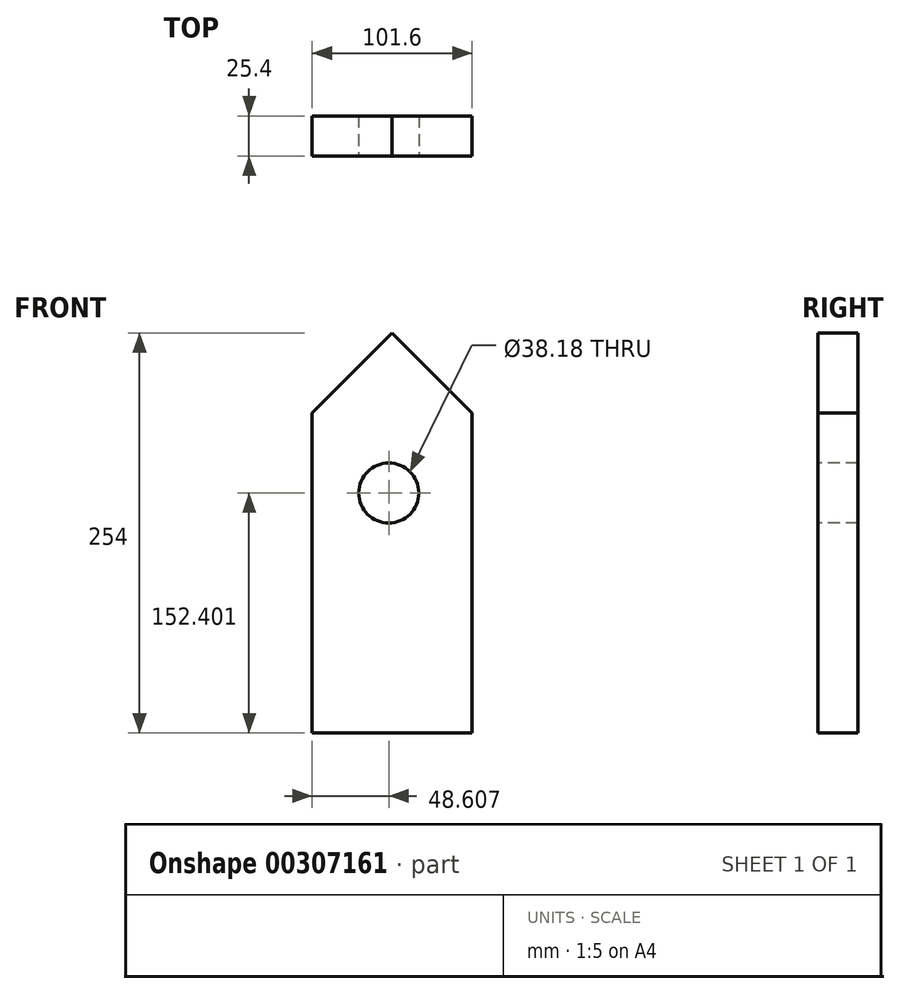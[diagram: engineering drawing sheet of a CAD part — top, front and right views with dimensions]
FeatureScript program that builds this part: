
annotation { "Feature Type Name" : "Feature", "Feature Type Description" : "" }
export const myFeature = defineFeature(function(context is Context, id is Id, definition is map)
    precondition{}
    {
        {
            var Q0;
            Q0=qCreatedBy(makeId("Front.planeOp"),FACE);
            var sketch = newSketch(context, id + "F0", { "sketchPlane" : qUnion([Q0])});
            skLineSegment(sketch, "E0", {"start": v(-46.78, -67.94) * mm, "end": v(54.82, -67.94) * mm});
            skLineSegment(sketch, "E1", {"start": v(54.82, -67.94) * mm, "end": v(54.82, 135.26) * mm});
            skLineSegment(sketch, "E2", {"start": v(-46.78, -67.94) * mm, "end": v(-46.78, 135.26) * mm});
            skLineSegment(sketch, "E3", {"start": v(-46.78, 135.26) * mm, "end": v(4.02, 186.06) * mm});
            skLineSegment(sketch, "E4", {"start": v(4.02, 186.06) * mm, "end": v(54.82, 135.26) * mm});
            skLineSegment(sketch, "E5", {"start": v(-46.78, 135.26) * mm, "end": v(-46.78, 84.46) * mm});
            skLineSegment(sketch, "E6", {"start": v(54.82, 135.26) * mm, "end": v(54.82, 84.46) * mm});
            skPoint(sketch, "E7", {"position": v(1.83, 84.46) * mm});
            skCircle(sketch, "E8", {"center": v(1.83, 84.46) * mm, "radius": 19.1 * mm});
            skSolve(sketch);
        }
        {
            var Q0;
            Q0 = qSketchRegion(id + "F0", true);
            extrude(context, id + "F1", {"entities" : qUnion([Q0]), "oppositeDirection" : true, "depth" : 25.4 * mm});
        }
    });
